# Revit family: Sileo DC 100
name_source: partatom
category: Оборудование
units: mm (PartAtom-declared; Revit-internal decimal feet)

## family parameters
Всегда вертикально = Да
Классификация = Нет
На основе рабочей плоскости = Нет
Общий = Нет
При загрузке вырезать с полостями = Нет
Размер круглого соединителя = Использовать диаметр
Тип детали = Нормальный
Точка принадлежности помещению = Нет

## types (1)
- Sileo DC 100
    00_20_Manufacturer = Blauberg
    00_20_Name = Axial fan
    00_20_Type = Sileo DC 100
    Amperage = 0.137 А
    Apparent Load = 32 Вт
    B = 158 мм
    Casing Material = Plastic, white
    D = 100 мм
    Diameter = 100 мм
    Dn = 104 мм
    Frequency = 50 Гц
    Height = 158 мм
    L = 107 мм
    L1 = 26 мм
    L2 = 81 мм
    L22 = 54 мм
    Length = 107 мм
    Load Classification = HVAC
    Maintenance zone material = <По категории>
    Maximum Air Flow = 101.0 м³/ч
    Number of Fase = 1
    Power = 4 Вт
    Sound pressure level at 3 m distance = 27 dBA
    URL = https://blaubergventilatoren.de
    Voltage = 230 В
    Width = 158 мм
    Изготовитель = Blauberg
    Отметка по умолчанию = 0 мм
